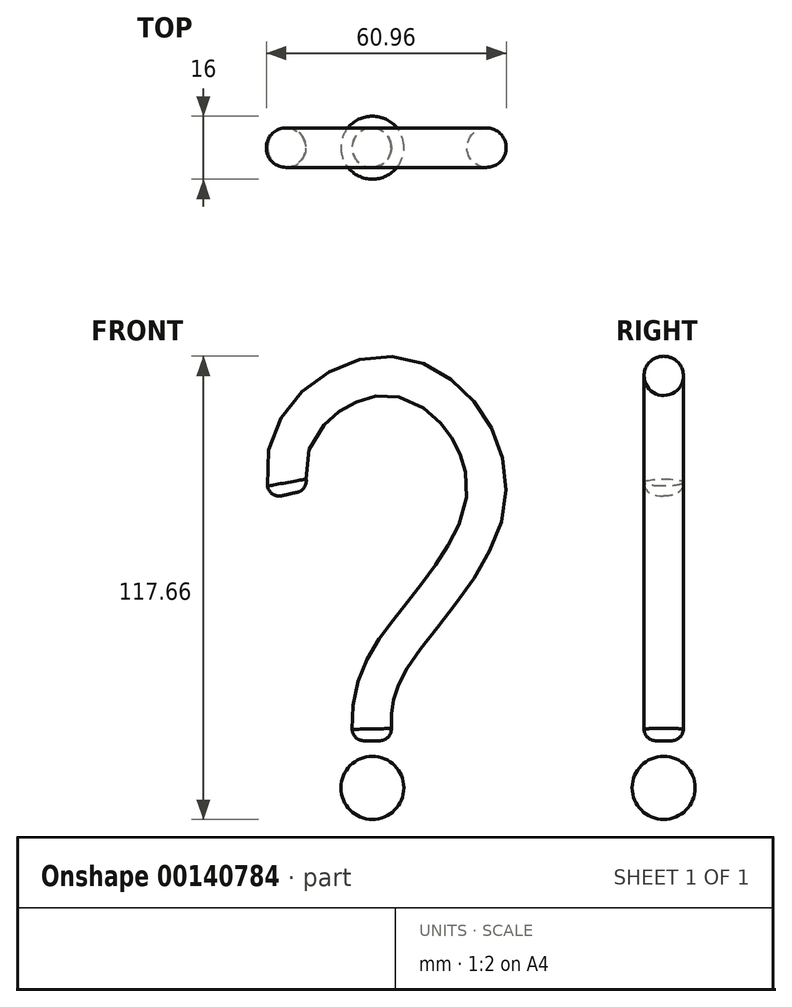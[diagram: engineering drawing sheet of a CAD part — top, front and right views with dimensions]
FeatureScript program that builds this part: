
annotation { "Feature Type Name" : "Feature", "Feature Type Description" : "" }
export const myFeature = defineFeature(function(context is Context, id is Id, definition is map)
    precondition{}
    {
        {
            var Q0;
            Q0=qCreatedBy(makeId("Front.planeOp"),FACE);
            var sketch = newSketch(context, id + "F0", { "sketchPlane" : qUnion([Q0])});
            skFitSpline(sketch, "E0", {"points": [v(-25, 0) * mm, v(0, 30) * mm, v(25, 0) * mm, v(0, -42.59) * mm, v(-3.96, -62.69) * mm], "startDerivative": vector(-57.73, 185.57) * mm, "endDerivative": vector(7.53, -101.97) * mm});
            skLineSegment(sketch, "E1", {"start": v(-47.83, 0) * mm, "end": v(41.13, 0) * mm, "construction": true});
            skLineSegment(sketch, "E2", {"start": v(0, 55) * mm, "end": v(0, -68.18) * mm, "construction": true});
            skSolve(sketch);
        }
        {
            var Q0;
            Q0=qCreatedBy(makeId("Top.planeOp"),FACE);
            var Q1;
            Q1=sQuery(id+"F0.wireOp",VERTEX,"E0.4.internal");
            cPlane(context, id + "F1", {"entities" : qUnion([Q0, Q1]), "cplaneType" : CPlaneType.PLANE_POINT, "offset" : 25 * mm, "oppositeDirection" : true, "width" : 150 * mm, "height" : 150 * mm});
        }
        {
            var Q0;
            Q0=qCreatedBy(id+"F1.planeOp",FACE);
            var sketch = newSketch(context, id + "F2", { "sketchPlane" : qUnion([Q0])});
            skCircle(sketch, "E3", {"center": v(-3.96, 0) * mm, "radius": 5 * mm});
            skSolve(sketch);
        }
        {
            var Q0;
            Q0=makeQuery(id+"F2.imprint","IMPRINT",FACE,{"disambiguationData":[TD([[makeQuery(id+"F2.imprint","IMPRINT",EDGE,{"derivedFrom":sQuery(id+"F2.wireOp",EDGE,"E3")}),1.0]])]});
            var Q1;
            Q1=sQuery(id+"F0.wireOp",EDGE,"E0");
            sweep(context, id + "F3", {"profiles" : qUnion([Q0]), "path" : qUnion([Q1])});
        }
        {
            var Q0;
            Q0=qCreatedBy(makeId("Front.planeOp"),FACE);
            var sketch = newSketch(context, id + "F4", { "sketchPlane" : qUnion([Q0])});
            skLineSegment(sketch, "E4.0", {"start": v(-8.96, -62.69) * mm, "end": v(1.04, -62.69) * mm, "construction": true});
            skLineSegment(sketch, "E5", {"start": v(-3.96, -59.45) * mm, "end": v(-3.96, -97.35) * mm, "construction": true});
            skPoint(sketch, "E5.startSnap0", {"position": v(-3.96, -62.69) * mm});
            skLineSegment(sketch, "E6.bottom", {"start": v(-8.96, -74.69) * mm, "end": v(1.04, -74.69) * mm});
            skLineSegment(sketch, "E6.top", {"start": v(-8.96, -64.69) * mm, "end": v(1.04, -64.69) * mm});
            skLineSegment(sketch, "E6.left", {"start": v(-8.96, -74.69) * mm, "end": v(-8.96, -64.69) * mm});
            skLineSegment(sketch, "E6.right", {"start": v(1.04, -74.69) * mm, "end": v(1.04, -64.69) * mm});
            skPoint(sketch, "E6.middle", {"position": v(-3.96, -69.69) * mm});
            skSolve(sketch);
        }
        {
            var Q0;
            Q0=qCreatedBy(makeId("Front.planeOp"),FACE);
            var sketch = newSketch(context, id + "F5", { "sketchPlane" : qUnion([Q0])});
            skLineSegment(sketch, "E7.0", {"start": v(-3.96, -59.45) * mm, "end": v(-3.96, -97.35) * mm, "construction": true});
            skArc(sketch, "E8", {"start": v(4.04, -74.66) * mm, "mid": v(-3.96, -66.66) * mm, "end": v(-11.96, -74.66) * mm});
            skLineSegment(sketch, "E9", {"start": v(-11.96, -74.66) * mm, "end": v(4.04, -74.66) * mm});
            skLineSegment(sketch, "E10", {"start": v(-13.72, -74.66) * mm, "end": v(0.72, -74.66) * mm, "construction": true});
            skSolve(sketch);
        }
        {
            var Q0;
            Q0 = qSketchRegion(id + "F5", true);
            var Q1;
            Q1=sQuery(id+"F5.wireOp",EDGE,"E10");
            revolve(context, id + "F6", {"entities" : qUnion([Q0]), "axis" : qUnion([Q1]), "revolveType" : RevolveType.FULL});
        }
        {
            var Q0;
            Q0=makeQuery(id+"F3.opSweep","CAP_EDGE",EDGE,{"disambiguationData":[OSD([sQuery(id+"F0.wireOp",VERTEX,"E0.end"),sQuery(id+"F2.wireOp",EDGE,"E3")])],"isStart":true});
            var Q1;
            Q1=makeQuery(id+"F3.opSweep","CAP_EDGE",EDGE,{"disambiguationData":[OSD([sQuery(id+"F0.wireOp",VERTEX,"E0.start"),sQuery(id+"F2.wireOp",EDGE,"E3")])],"isStart":false});
            fillet(context, id + "F7", {"entities" : qUnion([Q0, Q1]), "radius" : 3 * mm, "tangentPropagation" : true, "allowEdgeOverflow" : false});
        }
    });
